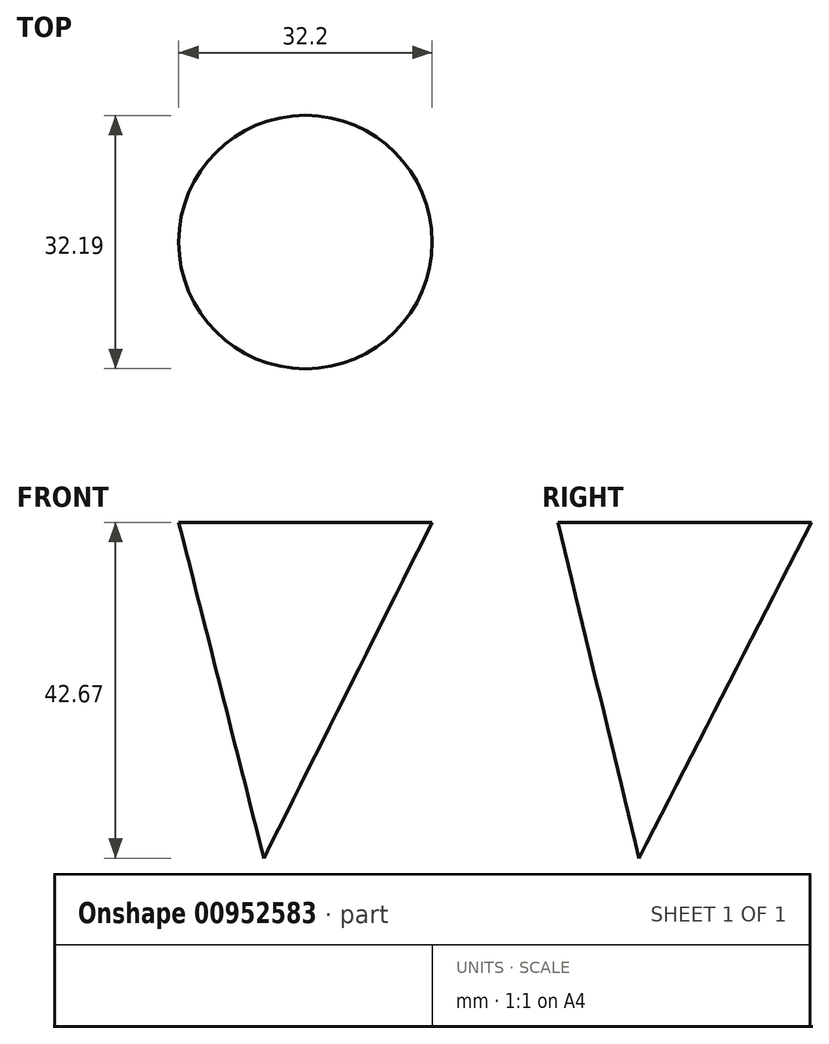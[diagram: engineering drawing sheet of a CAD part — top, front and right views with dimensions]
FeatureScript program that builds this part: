
annotation { "Feature Type Name" : "Feature", "Feature Type Description" : "" }
export const myFeature = defineFeature(function(context is Context, id is Id, definition is map)
    precondition{}
    {
        {
            var Q0;
            Q0=qCreatedBy(makeId("Top.planeOp"),FACE);
            var sketch = newSketch(context, id + "F0", { "sketchPlane" : qUnion([Q0])});
            skLineSegment(sketch, "E0", {"start": v(-39.9, 30.25) * mm, "end": v(-30.05, 45.62) * mm});
            skLineSegment(sketch, "E1", {"start": v(-30.05, 45.62) * mm, "end": v(-14.29, 45.62) * mm});
            skLineSegment(sketch, "E2", {"start": v(-14.29, 45.62) * mm, "end": v(-11.33, 40.1) * mm});
            skLineSegment(sketch, "E3", {"start": v(-11.33, 40.1) * mm, "end": v(-6.6, 45.62) * mm});
            skLineSegment(sketch, "E4", {"start": v(-6.4, 46.6) * mm, "end": v(-3.25, 33) * mm});
            skLineSegment(sketch, "E5", {"start": v(-3.25, 33) * mm, "end": v(4.43, 33) * mm});
            skLineSegment(sketch, "E6", {"start": v(4.43, 33) * mm, "end": v(-8.57, 23.75) * mm});
            skLineSegment(sketch, "E7", {"start": v(-8.57, 23.75) * mm, "end": v(-17.83, 19.6) * mm});
            skLineSegment(sketch, "E8", {"start": v(-17.83, 19.6) * mm, "end": v(-21.36, 27.5) * mm});
            skLineSegment(sketch, "E9", {"start": v(-21.58, 27.5) * mm, "end": v(-32.61, 19.6) * mm});
            skLineSegment(sketch, "E10", {"start": v(-32.61, 20.2) * mm, "end": v(-32.61, 28.28) * mm});
            skLineSegment(sketch, "E11", {"start": v(-32.61, 28.28) * mm, "end": v(-39.9, 30.25) * mm});
            skSolve(sketch);
        }
        {
            var Q0;
            Q0=qCreatedBy(makeId("Top.planeOp"),FACE);
            cPlane(context, id + "F1", {"entities" : qUnion([Q0]), "cplaneType" : CPlaneType.OFFSET, "offset" : 42.67 * mm, "width" : 152.4 * mm, "height" : 152.4 * mm});
        }
        {
            var Q0;
            Q0=qCreatedBy(id+"F1.planeOp",FACE);
            var sketch = newSketch(context, id + "F2", { "sketchPlane" : qUnion([Q0])});
            skCircle(sketch, "E12", {"center": v(-16.08, 33.35) * mm, "radius": 16.1 * mm});
            skSolve(sketch);
        }
        {
            var Q0;
            Q0=makeQuery(id+"F2.imprint","IMPRINT",FACE,{"disambiguationData":[TD([[makeQuery(id+"F2.imprint","IMPRINT",EDGE,{"derivedFrom":sQuery(id+"F2.wireOp",EDGE,"E12")}),1.0]])]});
            var Q1;
            Q1=sQuery(id+"F0.wireOp",VERTEX,"E8.end");
            loft(context, id + "F3", {"sheetProfilesArray" : [{ "sheetProfileEntities" : qUnion([Q0]) }, { "sheetProfileEntities" : qUnion([Q1]) }]});
        }
    });
